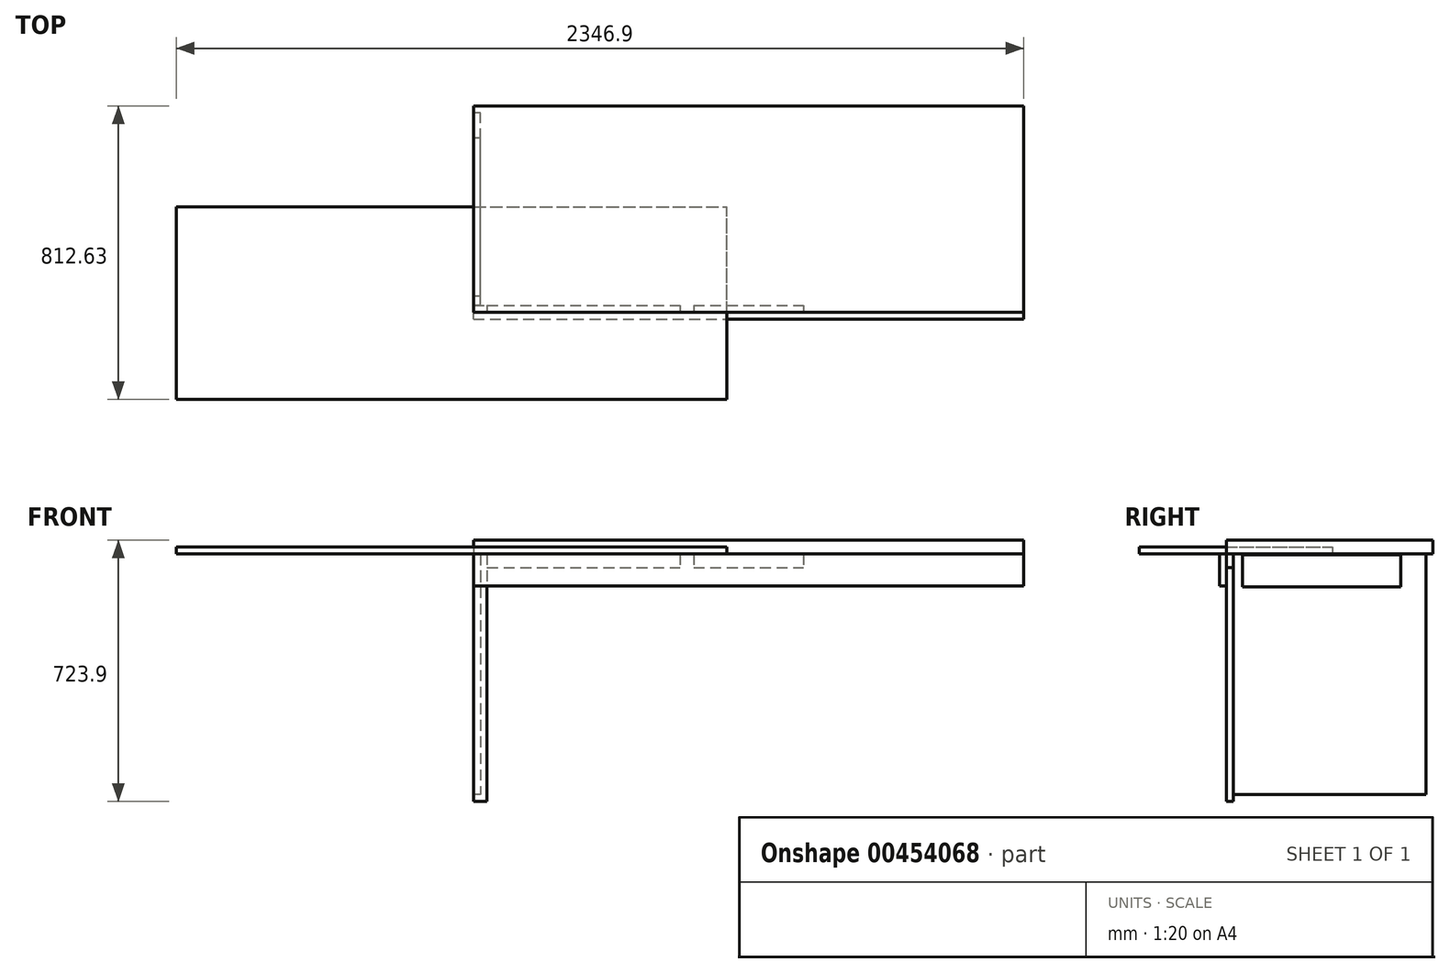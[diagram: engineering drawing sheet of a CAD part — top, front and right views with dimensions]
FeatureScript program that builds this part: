
annotation { "Feature Type Name" : "Feature", "Feature Type Description" : "" }
export const myFeature = defineFeature(function(context is Context, id is Id, definition is map)
    precondition{}
    {
        {
            var Q0;
            Q0=qCreatedBy(makeId("Top.planeOp"),FACE);
            var sketch = newSketch(context, id + "F0", { "sketchPlane" : qUnion([Q0])});
            skLineSegment(sketch, "E0.bottom", {"start": v(0, 0) * mm, "end": v(1524, 0) * mm});
            skLineSegment(sketch, "E0.top", {"start": v(0, 571.5) * mm, "end": v(1524, 571.5) * mm});
            skLineSegment(sketch, "E0.left", {"start": v(0, 0) * mm, "end": v(0, 571.5) * mm});
            skLineSegment(sketch, "E0.right", {"start": v(1524, 0) * mm, "end": v(1524, 571.5) * mm});
            skSolve(sketch);
        }
        {
            var Q0;
            Q0=makeQuery(id+"F0.imprint","IMPRINT",FACE,{"disambiguationData":[TD([[makeQuery(id+"F0.imprint","IMPRINT",EDGE,{"derivedFrom":sQuery(id+"F0.wireOp",EDGE,"E0.bottom")}),1.0]])]});
            var Q1;
            Q1 = qSketchRegion(id + "F2", true);
            extrude(context, id + "F1", {"entities" : qUnion([Q0, Q1]), "depth" : 38.1 * mm});
        }
        {
            var Q0;
            Q0=qCreatedBy(makeId("Front.planeOp"),FACE);
            var sketch = newSketch(context, id + "F2", { "sketchPlane" : qUnion([Q0])});
            skLineSegment(sketch, "E1.bottom", {"start": v(0, 0) * mm, "end": v(38.1, 0) * mm});
            skLineSegment(sketch, "E1.top", {"start": v(0, -685.8) * mm, "end": v(38.1, -685.8) * mm});
            skLineSegment(sketch, "E1.left", {"start": v(0, 0) * mm, "end": v(0, -685.8) * mm});
            skLineSegment(sketch, "E1.right", {"start": v(38.1, 0) * mm, "end": v(38.1, -685.8) * mm});
            skSolve(sketch);
        }
        {
            var Q0;
            Q0 = qSketchRegion(id + "F2", true);
            extrude(context, id + "F3", {"entities" : qUnion([Q0]), "oppositeDirection" : true, "depth" : 19.05 * mm});
        }
        {
            var Q0;
            Q0=qCreatedBy(makeId("Front.planeOp"),FACE);
            var sketch = newSketch(context, id + "F4", { "sketchPlane" : qUnion([Q0])});
            skLineSegment(sketch, "E2.bottom", {"start": v(38.1, 0) * mm, "end": v(571.5, 0) * mm});
            skLineSegment(sketch, "E2.top", {"start": v(38.1, -38.1) * mm, "end": v(571.5, -38.1) * mm});
            skLineSegment(sketch, "E2.left", {"start": v(38.1, 0) * mm, "end": v(38.1, -38.1) * mm});
            skLineSegment(sketch, "E2.right", {"start": v(571.5, 0) * mm, "end": v(571.5, -38.1) * mm});
            skSolve(sketch);
        }
        {
            var Q0;
            Q0=qCreatedBy(makeId("Front.planeOp"),FACE);
            var sketch = newSketch(context, id + "F5", { "sketchPlane" : qUnion([Q0])});
            skLineSegment(sketch, "E3.bottom", {"start": v(609.6, 0) * mm, "end": v(914.4, 0) * mm});
            skLineSegment(sketch, "E3.top", {"start": v(609.6, -38.1) * mm, "end": v(914.4, -38.1) * mm});
            skLineSegment(sketch, "E3.left", {"start": v(609.6, 0) * mm, "end": v(609.6, -38.1) * mm});
            skLineSegment(sketch, "E3.right", {"start": v(914.4, 0) * mm, "end": v(914.4, -38.1) * mm});
            skSolve(sketch);
        }
        {
            var Q0;
            Q0=makeQuery(id+"F4.imprint","IMPRINT",FACE,{"disambiguationData":[TD([[makeQuery(id+"F4.imprint","IMPRINT",EDGE,{"derivedFrom":sQuery(id+"F4.wireOp",EDGE,"E2.bottom")}),-1.0]])]});
            extrude(context, id + "F6", {"entities" : qUnion([Q0]), "oppositeDirection" : true, "depth" : 19.05 * mm});
        }
        {
            var Q0;
            Q0=makeQuery(id+"F5.imprint","IMPRINT",FACE,{"disambiguationData":[TD([[makeQuery(id+"F5.imprint","IMPRINT",EDGE,{"derivedFrom":sQuery(id+"F5.wireOp",EDGE,"E3.bottom")}),-1.0]])]});
            extrude(context, id + "F7", {"entities" : qUnion([Q0]), "oppositeDirection" : true, "depth" : 19.05 * mm});
        }
        {
            var Q0;
            Q0=qCreatedBy(makeId("Right.planeOp"),FACE);
            var sketch = newSketch(context, id + "F8", { "sketchPlane" : qUnion([Q0])});
            skLineSegment(sketch, "E4.bottom", {"start": v(19.05, 0) * mm, "end": v(552.45, 0) * mm});
            skLineSegment(sketch, "E4.top", {"start": v(19.05, -666.75) * mm, "end": v(552.45, -666.75) * mm});
            skLineSegment(sketch, "E4.left", {"start": v(19.05, 0) * mm, "end": v(19.05, -666.75) * mm});
            skLineSegment(sketch, "E4.right", {"start": v(552.45, 0) * mm, "end": v(552.45, -666.75) * mm});
            skSolve(sketch);
        }
        {
            var Q0;
            Q0 = qSketchRegion(id + "F8", true);
            extrude(context, id + "F9", {"entities" : qUnion([Q0]), "depth" : 19.05 * mm});
        }
        {
            var Q0;
            Q0=qCreatedBy(makeId("Top.planeOp"),FACE);
            var sketch = newSketch(context, id + "F10", { "sketchPlane" : qUnion([Q0])});
            skLineSegment(sketch, "E5.bottom", {"start": v(-822.9, -241.13) * mm, "end": v(701.1, -241.13) * mm});
            skLineSegment(sketch, "E5.top", {"start": v(-822.9, 292.27) * mm, "end": v(701.1, 292.27) * mm});
            skLineSegment(sketch, "E5.left", {"start": v(-822.9, -241.13) * mm, "end": v(-822.9, 292.27) * mm});
            skLineSegment(sketch, "E5.right", {"start": v(701.1, -241.13) * mm, "end": v(701.1, 292.27) * mm});
            skSolve(sketch);
        }
        {
            var Q0;
            Q0=makeQuery(id+"F10.imprint","IMPRINT",FACE,{"disambiguationData":[TD([[makeQuery(id+"F10.imprint","IMPRINT",EDGE,{"derivedFrom":sQuery(id+"F10.wireOp",EDGE,"E5.bottom")}),1.0]])]});
            extrude(context, id + "F11", {"entities" : qUnion([Q0]), "depth" : 19.05 * mm});
        }
        {
            var Q0;
            Q0=qCreatedBy(makeId("Front.planeOp"),FACE);
            var sketch = newSketch(context, id + "F12", { "sketchPlane" : qUnion([Q0])});
            skLineSegment(sketch, "E6.bottom", {"start": v(0, 0) * mm, "end": v(1524, 0) * mm});
            skLineSegment(sketch, "E6.top", {"start": v(0, -88.9) * mm, "end": v(1524, -88.9) * mm});
            skLineSegment(sketch, "E6.left", {"start": v(0, 0) * mm, "end": v(0, -88.9) * mm});
            skLineSegment(sketch, "E6.right", {"start": v(1524, 0) * mm, "end": v(1524, -88.9) * mm});
            skSolve(sketch);
        }
        {
            var Q0;
            Q0 = qSketchRegion(id + "F12", true);
            extrude(context, id + "F13", {"entities" : qUnion([Q0]), "depth" : 19.05 * mm});
        }
        {
            var Q0;
            Q0=qCreatedBy(makeId("Right.planeOp"),FACE);
            var sketch = newSketch(context, id + "F14", { "sketchPlane" : qUnion([Q0])});
            skLineSegment(sketch, "E7.bottom", {"start": v(44.45, -2.35) * mm, "end": v(482.6, -2.35) * mm});
            skLineSegment(sketch, "E7.top", {"start": v(44.45, -91.25) * mm, "end": v(482.6, -91.25) * mm});
            skLineSegment(sketch, "E7.left", {"start": v(44.45, -2.35) * mm, "end": v(44.45, -91.25) * mm});
            skLineSegment(sketch, "E7.right", {"start": v(482.6, -2.35) * mm, "end": v(482.6, -91.25) * mm});
            skSolve(sketch);
        }
        {
            var Q0;
            Q0=makeQuery(id+"F14.imprint","IMPRINT",FACE,{"disambiguationData":[TD([[makeQuery(id+"F14.imprint","IMPRINT",EDGE,{"derivedFrom":sQuery(id+"F14.wireOp",EDGE,"E7.bottom")}),-1.0]])]});
            extrude(context, id + "F15", {"entities" : qUnion([Q0]), "depth" : 19.05 * mm});
        }
    });
